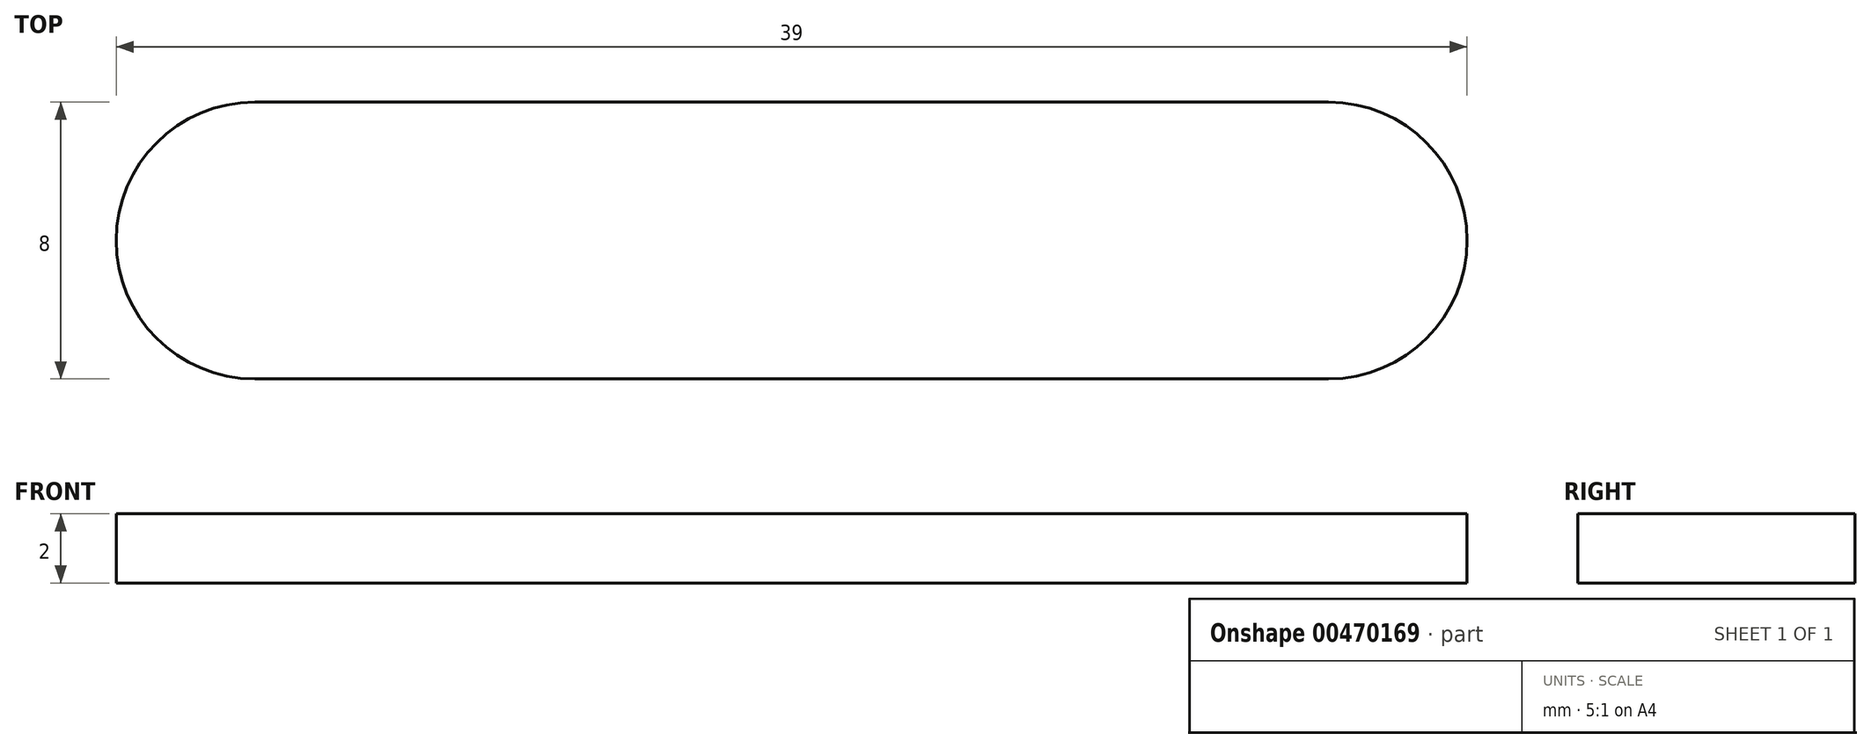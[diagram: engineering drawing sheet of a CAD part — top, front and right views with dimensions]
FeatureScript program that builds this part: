
annotation { "Feature Type Name" : "Feature", "Feature Type Description" : "" }
export const myFeature = defineFeature(function(context is Context, id is Id, definition is map)
    precondition{}
    {
        {
            var Q0;
            Q0=qCreatedBy(makeId("Top.planeOp"),FACE);
            var sketch = newSketch(context, id + "F0", { "sketchPlane" : qUnion([Q0])});
            skLineSegment(sketch, "E0.bottom", {"start": v(15.5, -4) * mm, "end": v(-15.5, -4) * mm});
            skLineSegment(sketch, "E0.top", {"start": v(15.5, 4) * mm, "end": v(-15.5, 4) * mm});
            skPoint(sketch, "E0.middle", {"position": v(0, 0) * mm});
            skArc(sketch, "E1", {"start": v(-15.5, 4) * mm, "mid": v(-19.5, 0) * mm, "end": v(-15.5, -4) * mm});
            skArc(sketch, "E2", {"start": v(15.5, -4) * mm, "mid": v(19.5, 0) * mm, "end": v(15.5, 4) * mm});
            skSolve(sketch);
        }
        {
            var Q0;
            Q0 = qSketchRegion(id + "F0", true);
            extrude(context, id + "F1", {"entities" : qUnion([Q0]), "depth" : 2 * mm});
        }
    });
